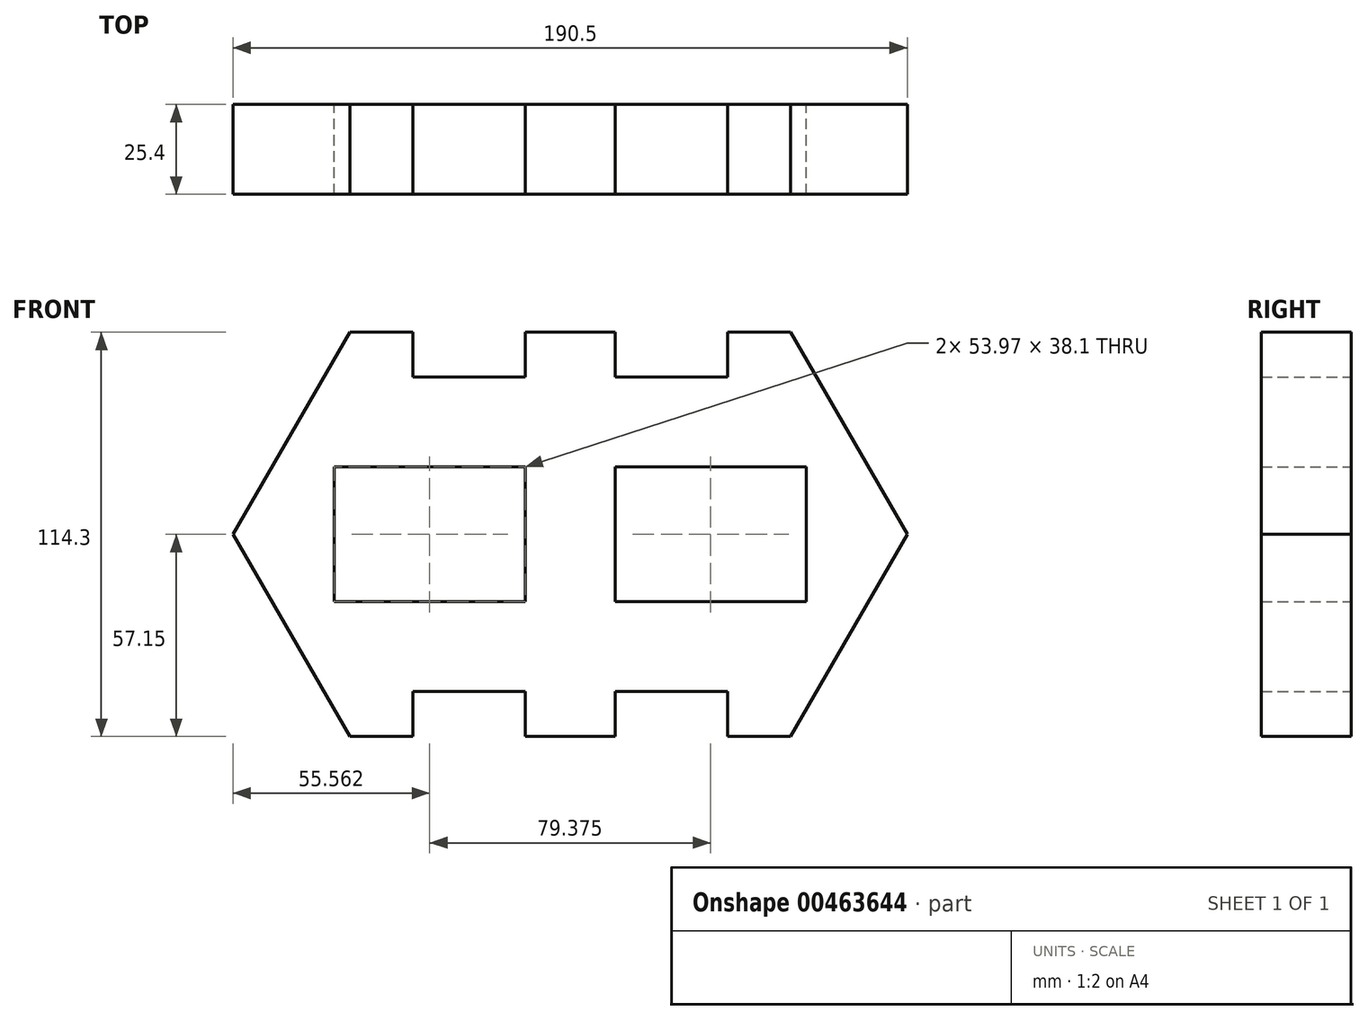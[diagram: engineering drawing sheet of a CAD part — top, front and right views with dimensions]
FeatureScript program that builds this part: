
annotation { "Feature Type Name" : "Feature", "Feature Type Description" : "" }
export const myFeature = defineFeature(function(context is Context, id is Id, definition is map)
    precondition{}
    {
        {
            var Q0;
            Q0=qCreatedBy(makeId("Front.planeOp"),FACE);
            var sketch = newSketch(context, id + "F0", { "sketchPlane" : qUnion([Q0])});
            skLineSegment(sketch, "E0.bottom", {"start": v(-62.25, 57.15) * mm, "end": v(-44.45, 57.15) * mm});
            skLineSegment(sketch, "E0.top", {"start": v(-62.25, -57.15) * mm, "end": v(-44.45, -57.15) * mm});
            skPoint(sketch, "E0.middle", {"position": v(0, 0) * mm});
            skLineSegment(sketch, "E1", {"start": v(-95.25, 0) * mm, "end": v(-62.25, 57.15) * mm});
            skLineSegment(sketch, "E2", {"start": v(-44.45, 57.15) * mm, "end": v(-44.45, 44.45) * mm});
            skLineSegment(sketch, "E3", {"start": v(-44.45, 44.45) * mm, "end": v(-12.7, 44.45) * mm});
            skLineSegment(sketch, "E4", {"start": v(-12.7, 44.45) * mm, "end": v(-12.7, 57.15) * mm});
            skLineSegment(sketch, "E5", {"start": v(-12.7, 57.15) * mm, "end": v(12.7, 57.15) * mm});
            skLineSegment(sketch, "E6", {"start": v(12.7, 57.15) * mm, "end": v(12.7, 44.45) * mm});
            skLineSegment(sketch, "E7", {"start": v(12.7, 44.45) * mm, "end": v(44.45, 44.45) * mm});
            skLineSegment(sketch, "E8", {"start": v(44.45, 44.45) * mm, "end": v(44.45, 57.15) * mm});
            skLineSegment(sketch, "E9", {"start": v(44.45, 57.15) * mm, "end": v(62.25, 57.15) * mm});
            skLineSegment(sketch, "E10", {"start": v(62.25, 57.15) * mm, "end": v(95.25, 0) * mm});
            skLineSegment(sketch, "E11", {"start": v(95.25, 0) * mm, "end": v(62.25, -57.15) * mm});
            skLineSegment(sketch, "E12", {"start": v(62.25, -57.15) * mm, "end": v(44.45, -57.15) * mm});
            skLineSegment(sketch, "E13", {"start": v(44.45, -57.15) * mm, "end": v(44.45, -44.45) * mm});
            skLineSegment(sketch, "E14", {"start": v(44.45, -44.45) * mm, "end": v(12.7, -44.45) * mm});
            skLineSegment(sketch, "E15", {"start": v(12.7, -44.45) * mm, "end": v(12.7, -57.15) * mm});
            skLineSegment(sketch, "E16", {"start": v(12.7, -57.15) * mm, "end": v(-12.7, -57.15) * mm});
            skLineSegment(sketch, "E17", {"start": v(-12.7, -57.15) * mm, "end": v(-12.7, -44.45) * mm});
            skLineSegment(sketch, "E18", {"start": v(-12.7, -44.45) * mm, "end": v(-44.45, -44.45) * mm});
            skLineSegment(sketch, "E19", {"start": v(-44.45, -44.45) * mm, "end": v(-44.45, -57.15) * mm});
            skLineSegment(sketch, "E20", {"start": v(-44.45, -57.15) * mm, "end": v(-62.25, -57.15) * mm});
            skLineSegment(sketch, "E21", {"start": v(-62.25, -57.15) * mm, "end": v(-95.25, 0) * mm});
            skLineSegment(sketch, "E22", {"start": v(-12.7, 19.05) * mm, "end": v(-12.7, -19.05) * mm});
            skLineSegment(sketch, "E23", {"start": v(-12.7, -19.05) * mm, "end": v(-66.68, -19.05) * mm});
            skLineSegment(sketch, "E24", {"start": v(-66.68, -19.05) * mm, "end": v(-66.68, 19.05) * mm});
            skLineSegment(sketch, "E25", {"start": v(-66.68, 19.05) * mm, "end": v(-12.7, 19.05) * mm});
            skPoint(sketch, "E26.endSnap0", {"position": v(12.7, 50.8) * mm});
            skLineSegment(sketch, "E27", {"start": v(12.7, 19.05) * mm, "end": v(66.67, 19.05) * mm});
            skLineSegment(sketch, "E28", {"start": v(66.67, 19.05) * mm, "end": v(66.67, -19.05) * mm});
            skLineSegment(sketch, "E29", {"start": v(66.67, -19.05) * mm, "end": v(12.7, -19.05) * mm});
            skLineSegment(sketch, "E30", {"start": v(12.7, -19.05) * mm, "end": v(12.7, 19.05) * mm});
            skPoint(sketch, "E31.orphan", {"position": v(-95.25, 57.15) * mm});
            skPoint(sketch, "E32.orphan", {"position": v(-95.25, -57.15) * mm});
            skPoint(sketch, "E33.orphan", {"position": v(95.25, -57.15) * mm});
            skPoint(sketch, "E34.orphan", {"position": v(95.25, 57.15) * mm});
            skLineSegment(sketch, "E35.trimOffspring", {"start": v(-12.7, -57.15) * mm, "end": v(12.7, -57.15) * mm});
            skLineSegment(sketch, "E36.trimOffspring", {"start": v(44.45, -57.15) * mm, "end": v(62.25, -57.15) * mm});
            skLineSegment(sketch, "E37", {"start": v(-95.25, 0) * mm, "end": v(-95.25, 33.83) * mm});
            skLineSegment(sketch, "E38", {"start": v(-62.25, 57.15) * mm, "end": v(-85.65, 57.15) * mm});
            skLineSegment(sketch, "E39", {"start": v(-95.25, 0) * mm, "end": v(-95.25, -33.45) * mm});
            skLineSegment(sketch, "E40", {"start": v(-62.25, -57.15) * mm, "end": v(-84.3, -57.15) * mm});
            skLineSegment(sketch, "E41", {"start": v(62.25, -57.15) * mm, "end": v(84.58, -57.15) * mm});
            skLineSegment(sketch, "E42", {"start": v(62.25, 57.15) * mm, "end": v(80.06, 57.15) * mm});
            skSolve(sketch);
        }
        {
            var Q0;
            Q0=makeQuery(id+"F0.imprint","IMPRINT",FACE,{"disambiguationData":[TD([[makeQuery(id+"F0.imprint","IMPRINT",EDGE,{"derivedFrom":sQuery(id+"F0.wireOp",EDGE,"E1")}),-1.0]])]});
            extrude(context, id + "F1", {"entities" : qUnion([Q0]), "depth" : 25.4 * mm, "symmetric" : true});
        }
    });
